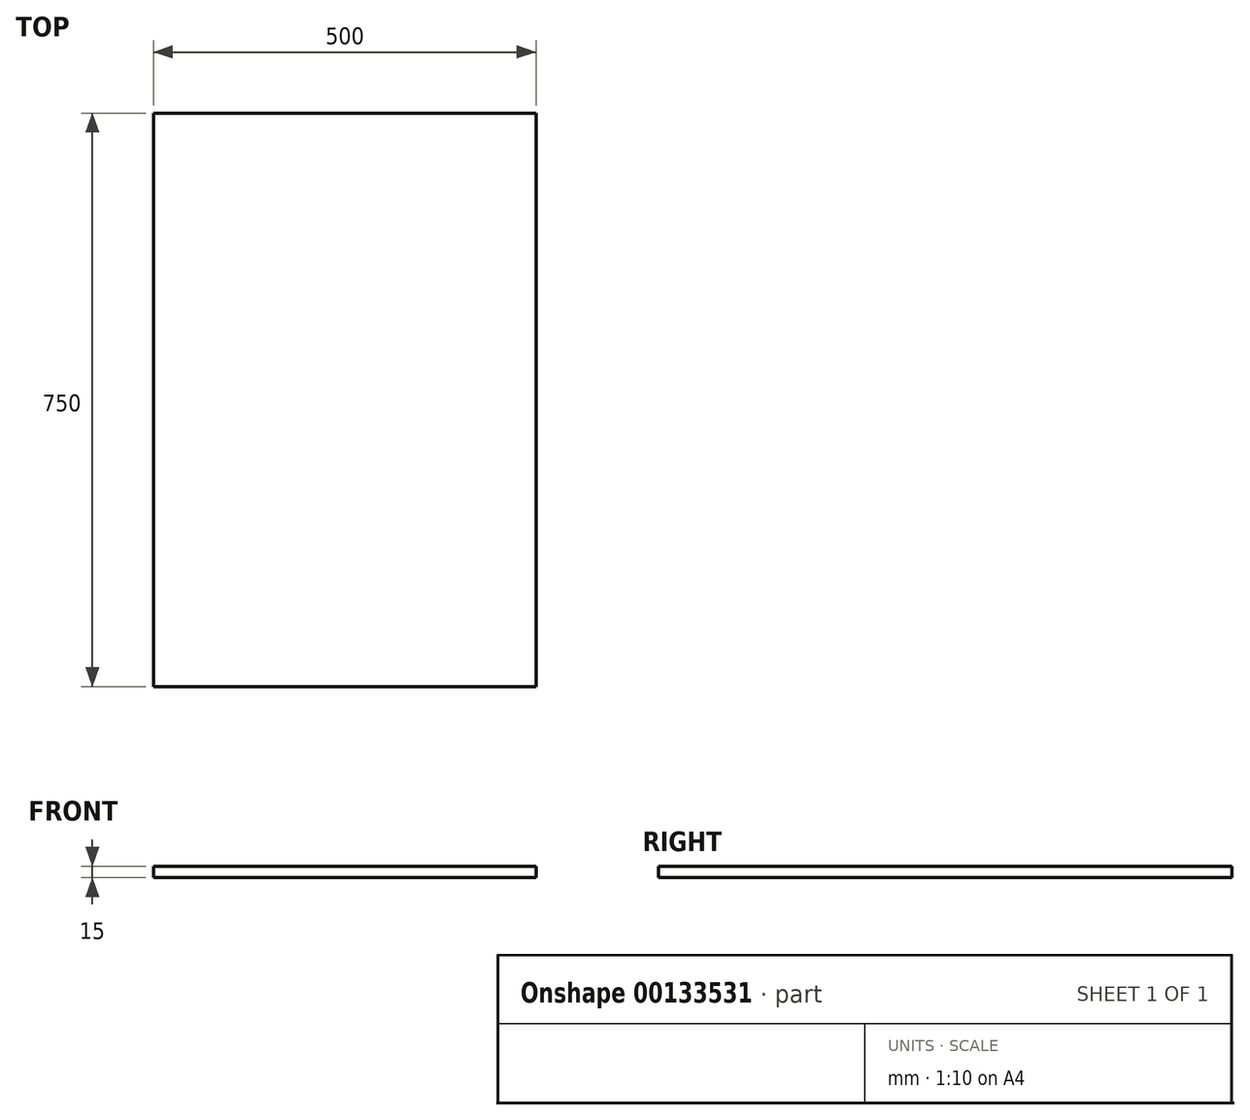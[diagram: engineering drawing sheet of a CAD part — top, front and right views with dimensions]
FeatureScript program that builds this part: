
annotation { "Feature Type Name" : "Feature", "Feature Type Description" : "" }
export const myFeature = defineFeature(function(context is Context, id is Id, definition is map)
    precondition{}
    {
        {
            var Q0;
            Q0=qCreatedBy(makeId("Right.planeOp"),FACE);
            var sketch = newSketch(context, id + "F0", { "sketchPlane" : qUnion([Q0])});
            skLineSegment(sketch, "E0.bottom", {"start": v(-375, 7.5) * mm, "end": v(375, 7.5) * mm});
            skLineSegment(sketch, "E0.top", {"start": v(-375, -7.5) * mm, "end": v(375, -7.5) * mm});
            skLineSegment(sketch, "E0.left", {"start": v(-375, 7.5) * mm, "end": v(-375, -7.5) * mm});
            skLineSegment(sketch, "E0.right", {"start": v(375, 7.5) * mm, "end": v(375, -7.5) * mm});
            skPoint(sketch, "E0.middle", {"position": v(0, 0) * mm});
            skSolve(sketch);
        }
        {
            var Q0;
            Q0=makeQuery(id+"F0.imprint","IMPRINT",FACE,{"disambiguationData":[TD([[makeQuery(id+"F0.imprint","IMPRINT",EDGE,{"derivedFrom":sQuery(id+"F0.wireOp",EDGE,"E0.bottom")}),-1.0]])]});
            extrude(context, id + "F1", {"entities" : qUnion([Q0]), "depth" : 500 * mm});
        }
    });
